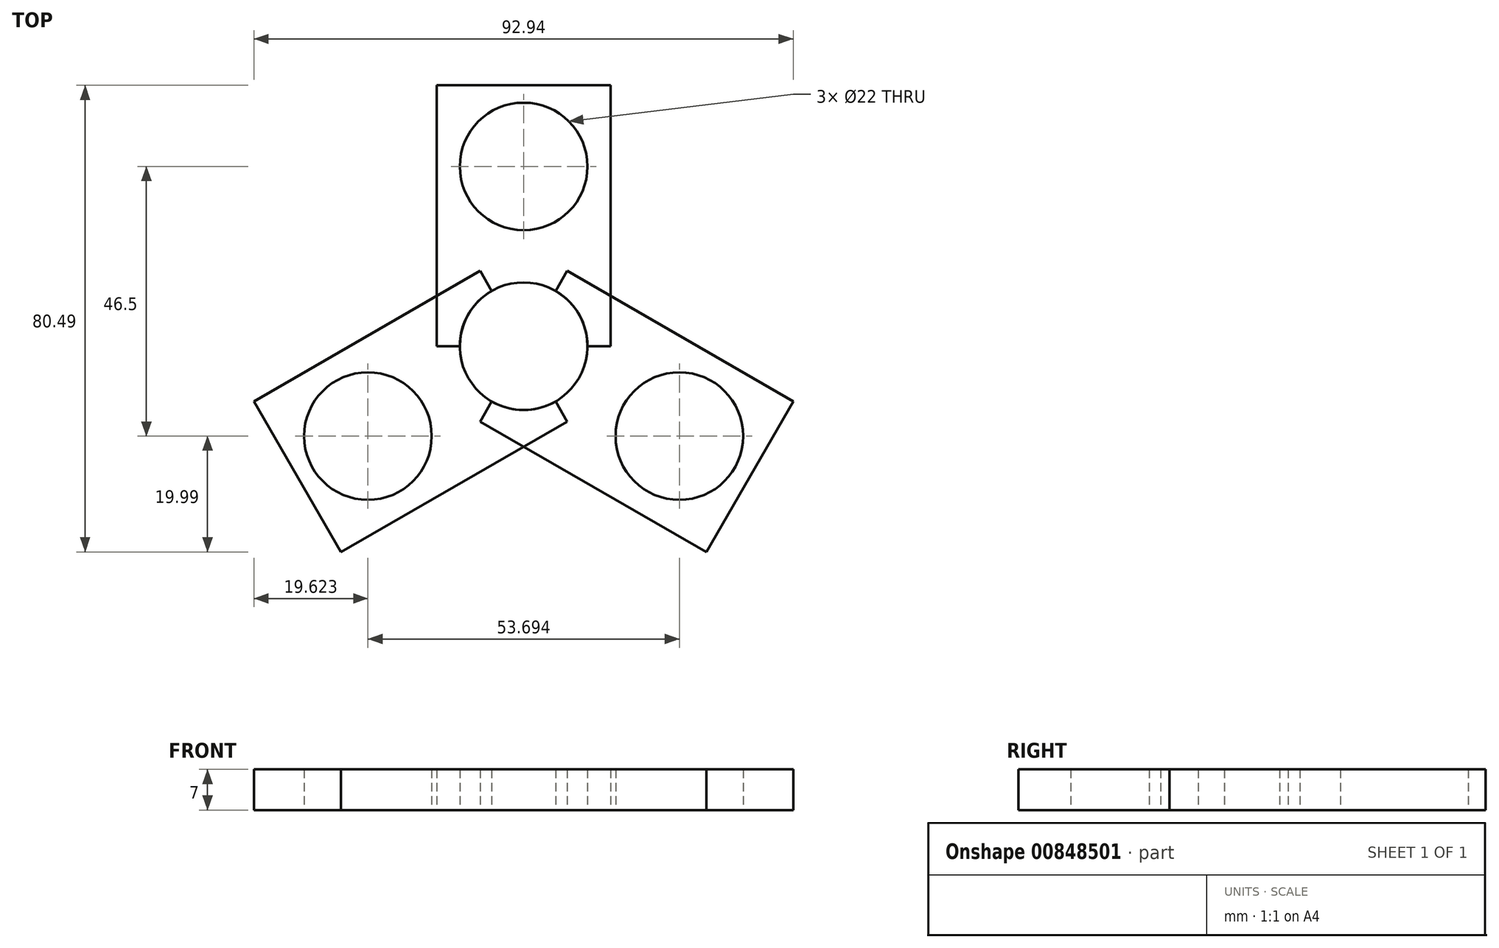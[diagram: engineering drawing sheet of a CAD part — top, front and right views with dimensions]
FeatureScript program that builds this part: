
annotation { "Feature Type Name" : "Feature", "Feature Type Description" : "" }
export const myFeature = defineFeature(function(context is Context, id is Id, definition is map)
    precondition{}
    {
        {
            var Q0;
            Q0=qCreatedBy(makeId("Top.planeOp"),FACE);
            var sketch = newSketch(context, id + "F0", { "sketchPlane" : qUnion([Q0])});
            skLineSegment(sketch, "E0", {"start": v(0, 0) * mm, "end": v(0, 45) * mm});
            skLineSegment(sketch, "E1", {"start": v(0, 45) * mm, "end": v(-15, 45) * mm});
            skLineSegment(sketch, "E2", {"start": v(0, 45) * mm, "end": v(15, 45) * mm});
            skLineSegment(sketch, "E3", {"start": v(-15, 45) * mm, "end": v(-15, 0) * mm});
            skLineSegment(sketch, "E4", {"start": v(-15, 0) * mm, "end": v(0, 0) * mm});
            skLineSegment(sketch, "E5", {"start": v(15, 45) * mm, "end": v(15, 0) * mm});
            skLineSegment(sketch, "E6", {"start": v(15, 0) * mm, "end": v(0, 0) * mm});
            skCircle(sketch, "E7", {"center": v(0, 0) * mm, "radius": 11 * mm});
            skLineSegment(sketch, "E8", {"start": v(0, 45) * mm, "end": v(0, 31) * mm});
            skCircle(sketch, "E9", {"center": v(0, 31) * mm, "radius": 11 * mm});
            skSolve(sketch);
        }
        {
            var Q0;
            {var subQ6=sQuery(id+"F0.wireOp",EDGE,"E1");Q0=makeQuery(id+"F0.imprint","IMPRINT",FACE,{"disambiguationData":[TD([[makeQuery(id+"F0.imprint","IMPRINT",EDGE,{"derivedFrom":subQ6}),1.0]])]});}
            var Q1;
            {var subQ4=sQuery(id+"F0.wireOp",EDGE,"E2");Q1=makeQuery(id+"F0.imprint","IMPRINT",FACE,{"disambiguationData":[TD([[makeQuery(id+"F0.imprint","IMPRINT",EDGE,{"derivedFrom":subQ4}),-1.0]])]});}
            extrude(context, id + "F1", {"entities" : qUnion([Q0, Q1]), "depth" : 7 * mm, "offsetDistance" : 25 * mm});
        }
        {
            var Q0;
            Q0=qCreatedBy(makeId("Right.planeOp"),FACE);
            var sketch = newSketch(context, id + "F2", { "sketchPlane" : qUnion([Q0])});
            skLineSegment(sketch, "E10", {"start": v(0, 0) * mm, "end": v(0, 23.66) * mm});
            skSolve(sketch);
        }
        {
            var Q0;
            Q0=makeQuery(id+"F1.opExtrude","SWEPT_BODY",BODY,{"disambiguationData":[OSD([sQuery(id+"F0.wireOp",EDGE,"E1"),sQuery(id+"F0.wireOp",EDGE,"E2"),sQuery(id+"F0.wireOp",EDGE,"E3"),sQuery(id+"F0.wireOp",EDGE,"E4"),sQuery(id+"F0.wireOp",EDGE,"E5"),sQuery(id+"F0.wireOp",EDGE,"E6"),sQuery(id+"F0.wireOp",EDGE,"E7"),sQuery(id+"F0.wireOp",EDGE,"E9")])]});
            var Q1;
            Q1=sQuery(id+"F2.wireOp",EDGE,"E10");
            transform(context, id + "F3", {"entities" : qUnion([Q0]), "transformType" : TransformType.ROTATION, "transformAxis" : qUnion([Q1]), "angle" : 120 * degree, "makeCopy" : true});
        }
        {
            var Q0;
            Q0=makeQuery(id+"F1.opExtrude","SWEPT_BODY",BODY,{"disambiguationData":[OSD([sQuery(id+"F0.wireOp",EDGE,"E1"),sQuery(id+"F0.wireOp",EDGE,"E2"),sQuery(id+"F0.wireOp",EDGE,"E3"),sQuery(id+"F0.wireOp",EDGE,"E4"),sQuery(id+"F0.wireOp",EDGE,"E5"),sQuery(id+"F0.wireOp",EDGE,"E6"),sQuery(id+"F0.wireOp",EDGE,"E7"),sQuery(id+"F0.wireOp",EDGE,"E9")])]});
            var Q1;
            Q1=sQuery(id+"F2.wireOp",EDGE,"E10");
            transform(context, id + "F4", {"entities" : qUnion([Q0]), "transformType" : TransformType.ROTATION, "transformAxis" : qUnion([Q1]), "angle" : 240 * degree, "makeCopy" : true});
        }
    });
